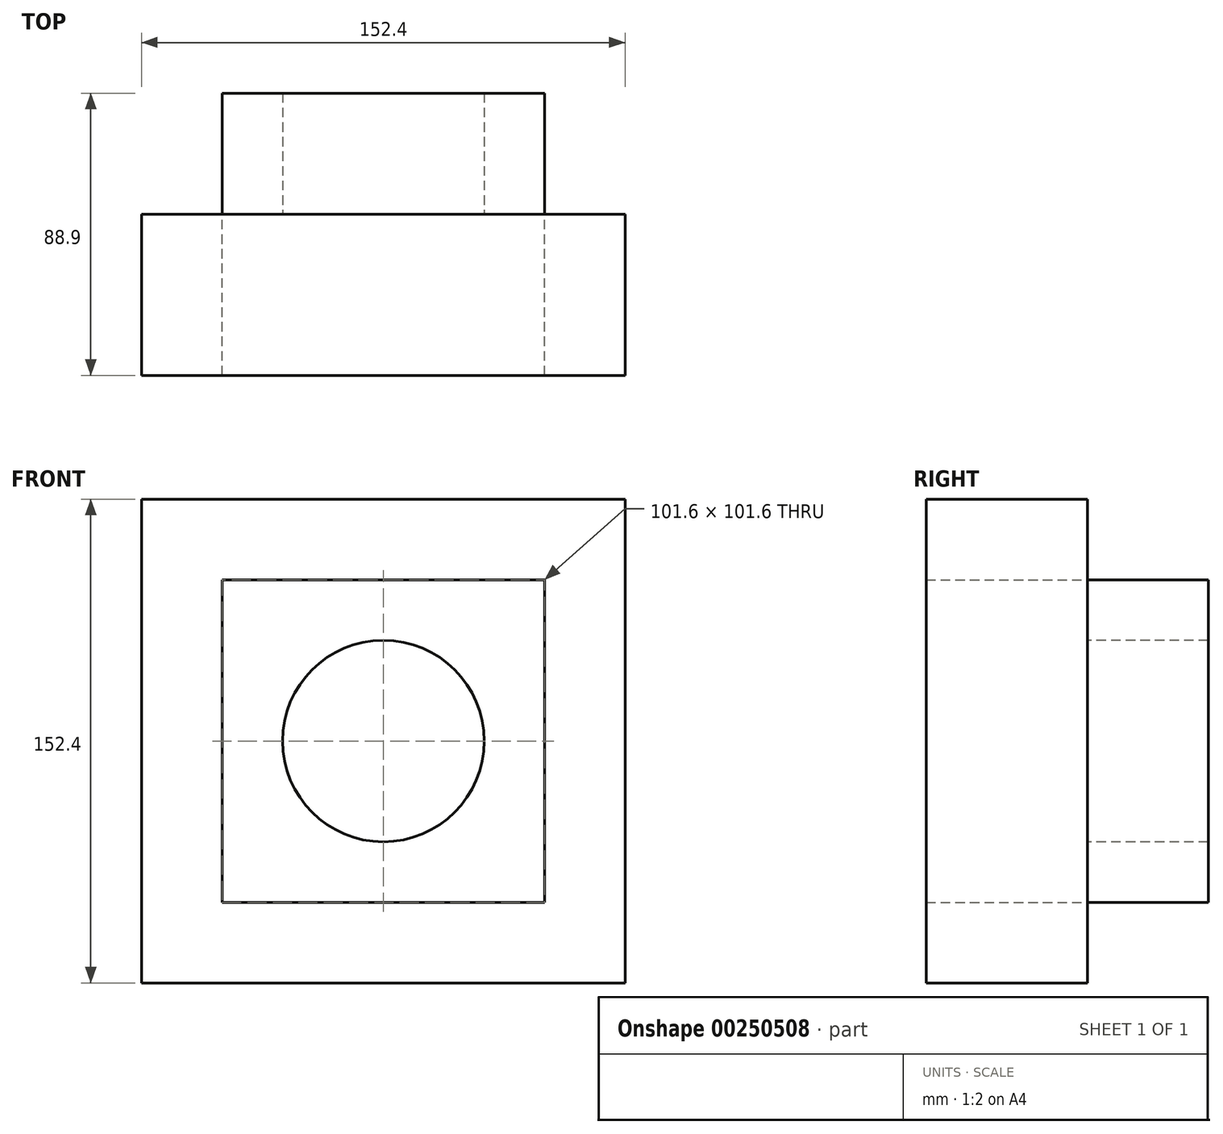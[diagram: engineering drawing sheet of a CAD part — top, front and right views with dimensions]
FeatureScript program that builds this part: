
annotation { "Feature Type Name" : "Feature", "Feature Type Description" : "" }
export const myFeature = defineFeature(function(context is Context, id is Id, definition is map)
    precondition{}
    {
        {
            var Q0;
            Q0=qCreatedBy(makeId("Front.planeOp"),FACE);
            var sketch = newSketch(context, id + "F0", { "sketchPlane" : qUnion([Q0])});
            skCircle(sketch, "E0", {"center": v(0, 0) * mm, "radius": 31.75 * mm});
            skLineSegment(sketch, "E1.bottom", {"start": v(50.8, 50.8) * mm, "end": v(-50.8, 50.8) * mm});
            skLineSegment(sketch, "E1.top", {"start": v(50.8, -50.8) * mm, "end": v(-50.8, -50.8) * mm});
            skLineSegment(sketch, "E1.left", {"start": v(50.8, 50.8) * mm, "end": v(50.8, -50.8) * mm});
            skLineSegment(sketch, "E1.right", {"start": v(-50.8, 50.8) * mm, "end": v(-50.8, -50.8) * mm});
            skLineSegment(sketch, "E2.bottom", {"start": v(76.2, 76.2) * mm, "end": v(-76.2, 76.2) * mm});
            skLineSegment(sketch, "E2.top", {"start": v(76.2, -76.2) * mm, "end": v(-76.2, -76.2) * mm});
            skLineSegment(sketch, "E2.left", {"start": v(76.2, 76.2) * mm, "end": v(76.2, -76.2) * mm});
            skLineSegment(sketch, "E2.right", {"start": v(-76.2, 76.2) * mm, "end": v(-76.2, -76.2) * mm});
            skSolve(sketch);
        }
        {
            var Q0;
            Q0=makeQuery(id+"F0.imprint","IMPRINT",FACE,{"disambiguationData":[TD([[makeQuery(id+"F0.imprint","IMPRINT",EDGE,{"derivedFrom":sQuery(id+"F0.wireOp",EDGE,"E1.bottom")}),-1.0]])]});
            extrude(context, id + "F1", {"entities" : qUnion([Q0]), "depth" : 50.8 * mm});
        }
        {
            var Q0;
            Q0=makeQuery(id+"F0.imprint","IMPRINT",FACE,{"disambiguationData":[TD([[makeQuery(id+"F0.imprint","IMPRINT",EDGE,{"derivedFrom":sQuery(id+"F0.wireOp",EDGE,"E0")}),-1.0]])]});
            extrude(context, id + "F2", {"entities" : qUnion([Q0]), "oppositeDirection" : true, "depth" : 38.1 * mm});
        }
    });
